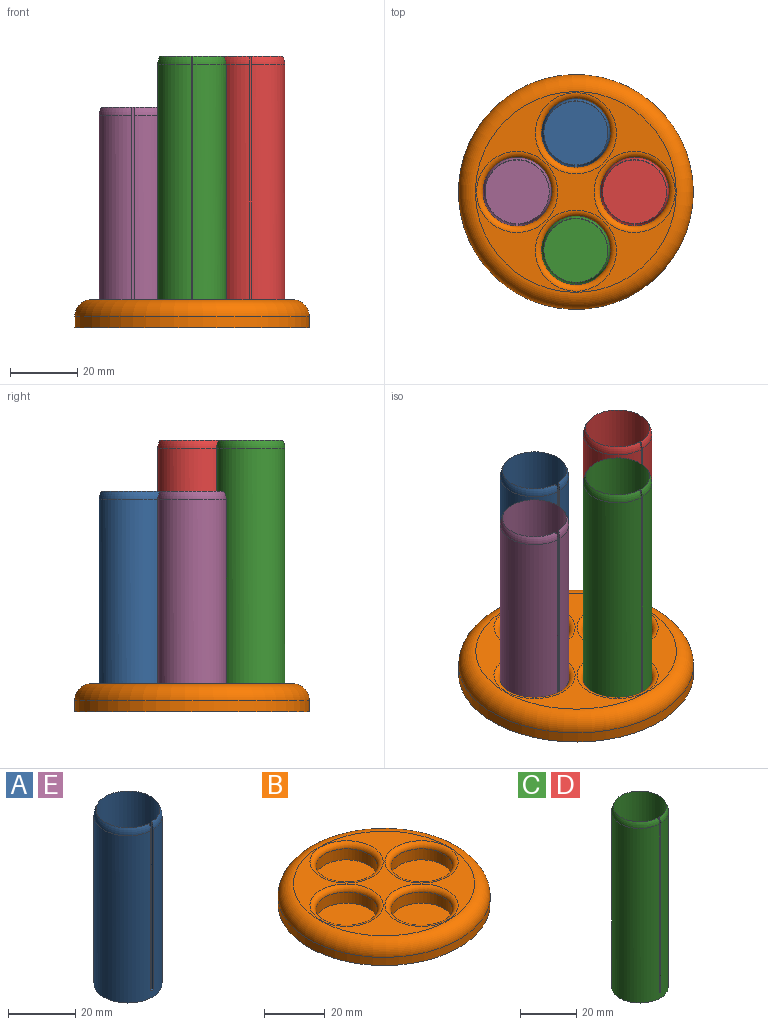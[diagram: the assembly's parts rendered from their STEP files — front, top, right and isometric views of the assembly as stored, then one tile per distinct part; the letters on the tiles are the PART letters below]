
ASSEMBLY  parts=5 mates=4
PART A: 7 faces, bbox 22x22x64.7 mm
  f0: cylinder r=10.16mm len=61.04mm, axis (0,0,-1), area 3837.6mm2, adj f1,f2,f3,f4,f6
  f1: plane 20.32x20.32mm, normal (0,0,-1), area 324.3mm2, adj f0
  f2: plane 19.69x19.05mm, normal (0,0,1), area 285.7mm2, adj f0,f3,f4,f5
  f3: plane 60.98x0.66mm, normal (-1,0,0), area 38.3mm2, adj f0,f2,f5,f6
  f4: plane 60.98x0.66mm, normal (1,0,0), area 38.3mm2, adj f0,f2,f5,f6
  f5: cylinder r=9.53mm len=60.96mm, axis (0,0,1), area 3586.8mm2, adj f2,f3,f4,f6
  f6: torus R=5.08mm, axis (0,0,1), area 157.8mm2, adj f0,f3,f4,f5
PART B: 16 faces, bbox 75.6x75.6x8.4 mm
  f0: cylinder r=34.92mm len=69.85mm, axis (0,0,-1), area 724.6mm2, adj f2,f11
  f1: plane 59.69x59.69mm, normal (0,0,1), area 969.1mm2, adj f11,f12,f13,f14,f15
  f2: plane 69.85x69.85mm, normal (0,0,-1), area 3832mm2, adj f0
  f3: cylinder r=10.16mm len=20.32mm, axis (0,0,1), area 283.8mm2, adj f4,f15
  f4: plane 20.32x20.32mm, normal (0,0,1), area 324.3mm2, adj f3
  f5: cylinder r=10.16mm len=20.32mm, axis (0,0,1), area 283.8mm2, adj f6,f12
  f6: plane 20.32x20.32mm, normal (0,0,1), area 324.3mm2, adj f5
  f7: cylinder r=10.16mm len=20.32mm, axis (0,0,1), area 283.8mm2, adj f8,f14
  f8: plane 20.32x20.32mm, normal (0,0,1), area 324.3mm2, adj f7
  f9: cylinder r=10.16mm len=20.32mm, axis (0,0,1), area 283.8mm2, adj f10,f13
  f10: plane 20.32x20.32mm, normal (0,0,1), area 324.3mm2, adj f9
  f11: torus R=29.84mm, axis (0,0,1), area 1658.5mm2, adj f0,f1
  f12: torus R=12.06mm, axis (0,0,1), area 204mm2, adj f1,f5
  f13: torus R=12.06mm, axis (0,0,1), area 204mm2, adj f1,f9
  f14: torus R=12.06mm, axis (0,0,1), area 204mm2, adj f1,f7
  f15: torus R=12.06mm, axis (0,0,1), area 204mm2, adj f1,f3
PART C: 7 faces, bbox 22x22x79.9 mm
  f0: cylinder r=10.16mm len=76.28mm, axis (0,0,-1), area 4830.9mm2, adj f1,f2,f3,f4,f6
  f1: plane 20.32x20.32mm, normal (0,0,-1), area 324.3mm2, adj f0
  f2: plane 19.69x19.05mm, normal (0,0,1), area 285.4mm2, adj f0,f3,f4,f5
  f3: plane 76.21x0.65mm, normal (-1,0,0), area 47.9mm2, adj f0,f2,f5,f6
  f4: plane 76.21x0.65mm, normal (1,0,0), area 47.9mm2, adj f0,f2,f5,f6
  f5: cylinder r=9.53mm len=76.2mm, axis (0,0,1), area 4520.4mm2, adj f2,f3,f4,f6
  f6: torus R=5.08mm, axis (0,0,1), area 159.1mm2, adj f0,f3,f4,f5
PART D: same geometry as C
PART E: same geometry as A
PLACE A t=(28.25,60.44,2.89)mm
PLACE B t=(28.25,42.97,0.86)mm
PLACE C t=(28.25,25.51,2.89)mm
PLACE D t=(45.71,42.97,2.89)mm
PLACE E t=(10.78,42.97,2.89)mm
MATE fastened E.f0 <-> B.f3  axis (0,0,-1) through (10.78,42.97,2.89)mm
MATE fastened C.f0 <-> B.f7  axis (0,0,-1) through (28.25,25.51,2.89)mm
MATE fastened D.f0 <-> B.f9  axis (0,0,-1) through (45.71,42.97,2.89)mm
MATE fastened A.f0 <-> B.f5  axis (0,0,-1) through (28.25,60.44,2.89)mm
